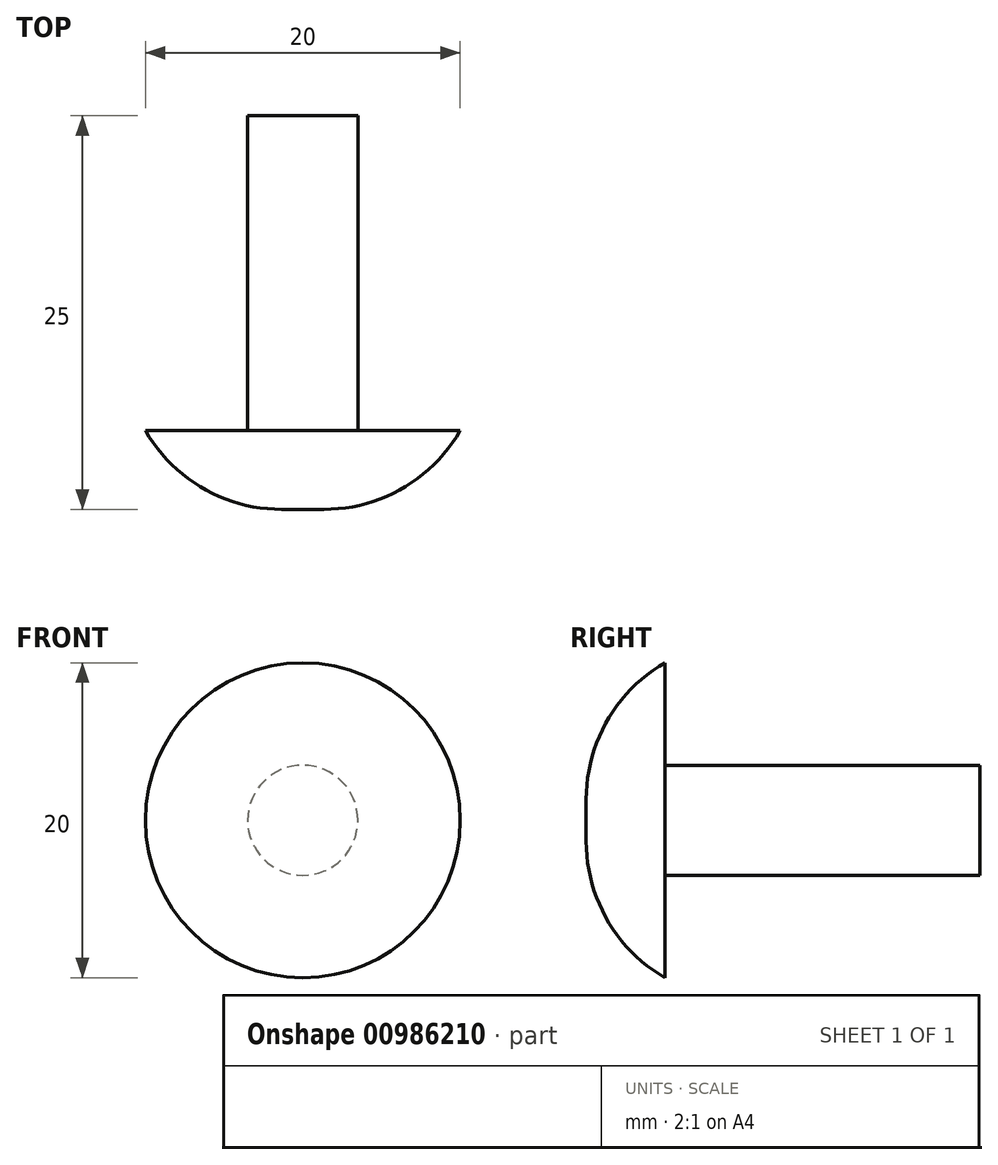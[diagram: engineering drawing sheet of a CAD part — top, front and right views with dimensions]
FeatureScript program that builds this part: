
annotation { "Feature Type Name" : "Feature", "Feature Type Description" : "" }
export const myFeature = defineFeature(function(context is Context, id is Id, definition is map)
    precondition{}
    {
        {
            var Q0;
            Q0=qCreatedBy(makeId("Front.planeOp"),FACE);
            var sketch = newSketch(context, id + "F0", { "sketchPlane" : qUnion([Q0])});
            skCircle(sketch, "E0", {"center": v(0, 0) * mm, "radius": 3.5 * mm});
            skSolve(sketch);
        }
        {
            var Q0;
            Q0=makeQuery(id+"F0.imprint","IMPRINT",FACE,{"disambiguationData":[TD([[makeQuery(id+"F0.imprint","IMPRINT",EDGE,{"derivedFrom":sQuery(id+"F0.wireOp",EDGE,"E0")}),1.0]])]});
            extrude(context, id + "F1", {"entities" : qUnion([Q0]), "depth" : 20 * mm, "offsetDistance" : 25 * mm});
        }
        {
            var Q0;
            Q0=makeQuery(id+"F1.opExtrude","CAP_FACE",FACE,{"disambiguationData":[OSD([sQuery(id+"F0.wireOp",EDGE,"E0")])],"isStart":false});
            var sketch = newSketch(context, id + "F2", { "sketchPlane" : qUnion([Q0])});
            skCircle(sketch, "E1", {"center": v(0, 0) * mm, "radius": 10 * mm});
            skSolve(sketch);
        }
        {
            var Q0;
            Q0=makeQuery(id+"F2.imprint","IMPRINT",FACE,{"disambiguationData":[TD([[makeQuery(id+"F2.imprint","IMPRINT",EDGE,{"derivedFrom":sQuery(id+"F2.wireOp",EDGE,"E1")}),1.0]])]});
            var Q1;
            Q1=makeQuery(id+"F2.imprint","IMPRINT",FACE,{"disambiguationData":[TD([[makeQuery(id+"F2.imprint","IMPRINT",EDGE,{"derivedFrom":makeQuery(id+"F1.opExtrude","CAP_EDGE",EDGE,{"disambiguationData":[OSD([sQuery(id+"F0.wireOp",EDGE,"E0")])],"isStart":false})}),1.0]])]});
            extrude(context, id + "F3", {"entities" : qUnion([Q0, Q1]), "operationType" : NewBodyOperationType.ADD, "depth" : 5 * mm, "offsetDistance" : 25 * mm});
        }
        {
            var Q0;
            Q0=makeQuery(id+"F3.opExtrude","CAP_EDGE",EDGE,{"disambiguationData":[OSD([sQuery(id+"F2.wireOp",EDGE,"E1")])],"isStart":false});
            fillet(context, id + "F4", {"entities" : qUnion([Q0]), "radius" : 10 * mm, "tangentPropagation" : true, "allowEdgeOverflow" : false});
        }
    });
